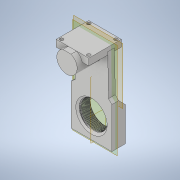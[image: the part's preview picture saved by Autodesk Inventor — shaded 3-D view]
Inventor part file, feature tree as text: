
AUTODESK INVENTOR PART (.ipt)
format: ipt  version: 2022 (Build 260153000, 153)  size: 550,400 bytes
history: native  units: mm
features: other x10, sketch x9, extrude x7, reference x5, plane x3, chamfer x2, helix x1, revolve x1, projected_geometry x1
ambient origin geometry x8: Origin, YZ Plane, XZ Plane, XY Plane, X Axis, Y Axis, Z Axis, Center Point
bodies: Solid1 (feature_tree)
feature tree (39):
  plane  "Work Plane1"
  extrude  "Extrusion1"  Depth=30.0mm
  extrude  "Extrusion2"  Depth=5.0mm TaperAngle=0.0deg
  plane  "Work Plane2"
  other  "Work Axis2"
  helix  "Coil1"  [1 undecoded]
  plane  "Work Plane3"
  extrude  "Extrusion11"  Depth=9.95mm
  extrude  "Extrusion12"  Depth=8.0mm
  revolve  "Revolution1"  [1 undecoded]
  extrude  "Extrusion13"  TaperAngle=45.0deg  [1 undecoded]
  chamfer  "Chamfer2"  Distance=12.0mm
  extrude  "Extrusion14"  Depth=15.0mm TaperAngle=0.0deg
  extrude  "Extrusion15"  Depth=5.0mm TaperAngle=45.0deg
  chamfer  "Chamfer1"  Distance=24.0mm
  sketch  "Sketch1"  dims[d0=25.0mm d1=30.0mm]
  sketch  "Sketch2"  dims[d2=30.0mm d3=5.0mm d4=0.0mm d5=21.0mm]
  reference  "Reference3"
  reference  "Reference4"
  sketch  "Sketch6"  dims[d6=5.0mm d7=0.0mm]
  reference  "Reference8"
  reference  "Reference9"
  sketch  "Sketch11"  dims[d16=0.15mm d17=0.0mm d18=120.0deg d19=0.15mm d20=120.0deg d21=1.0mm d22=0.713333mm]
  sketch  "Sketch12"  dims[d25=0.713333mm d26=10.0mm d27=135.0mm d28=0.0mm d29=90.0deg d30=90.0deg d31=0.0mm d32=0.0mm d33=9.95mm]
  projected_geometry  "Projected Loop5"
  sketch  "Sketch13"  dims[d48=5.0mm d49=0.0mm d50=8.0mm]
  sketch  "Sketch14"  dims[d51=8.0mm d52=5.0mm d53=0.0mm]
  reference  "Reference16"
  sketch  "Sketch15"  dims[d54=135.0deg d55=45.0deg]
  sketch  "Sketch16"  dims[d56=90.0deg d57=12.0mm d58=15.0mm d59=7.0mm d60=0.0mm d61=0.0mm d62=5.0mm d63=2.0mm d64=45.0deg d65=24.0mm d66=24.0mm d67=5.0mm d68=2.0mm d69=2.5mm d70=2.5mm d71=2.5mm d72=2.5mm d73=5.0mm d74=2.0mm d75=45.0deg d76=1.5mm d77=16.0mm d78=0.0mm d79=2.0mm d80=0.0mm]
  other  "Assembly_Cube_Z_Focus_MGN_NEMA_v3.iam"
  other  "00_Microscope_Objective_Lens10x:1"
  other  "Assembly_Cube_empty_IM_v3:2"
  other  "10_Cube_1x1_IM:1"
  other  "<userpath> Lab\Documents\UC2-INVENTOR-Git\uc2_v3\Assembly_Cube_SQUID_Z_Focus_v3.iam"
  other  "Assembly_Cube_SQUID_Z_Focus_v3.iam"
  other  "00_X-axis_MX25-SC:1"
  other  "AMETEK-21H4U-2_5-0_75-12-ENC:1"
  other  "30_Cube_Z_Focus_MGN_NEMA_slide:1"
note: 3 required parameter values undecoded (feature->parameter linkage not recoverable at this tier; creation-order binding heuristic only, values carry confidence <= 0.55)